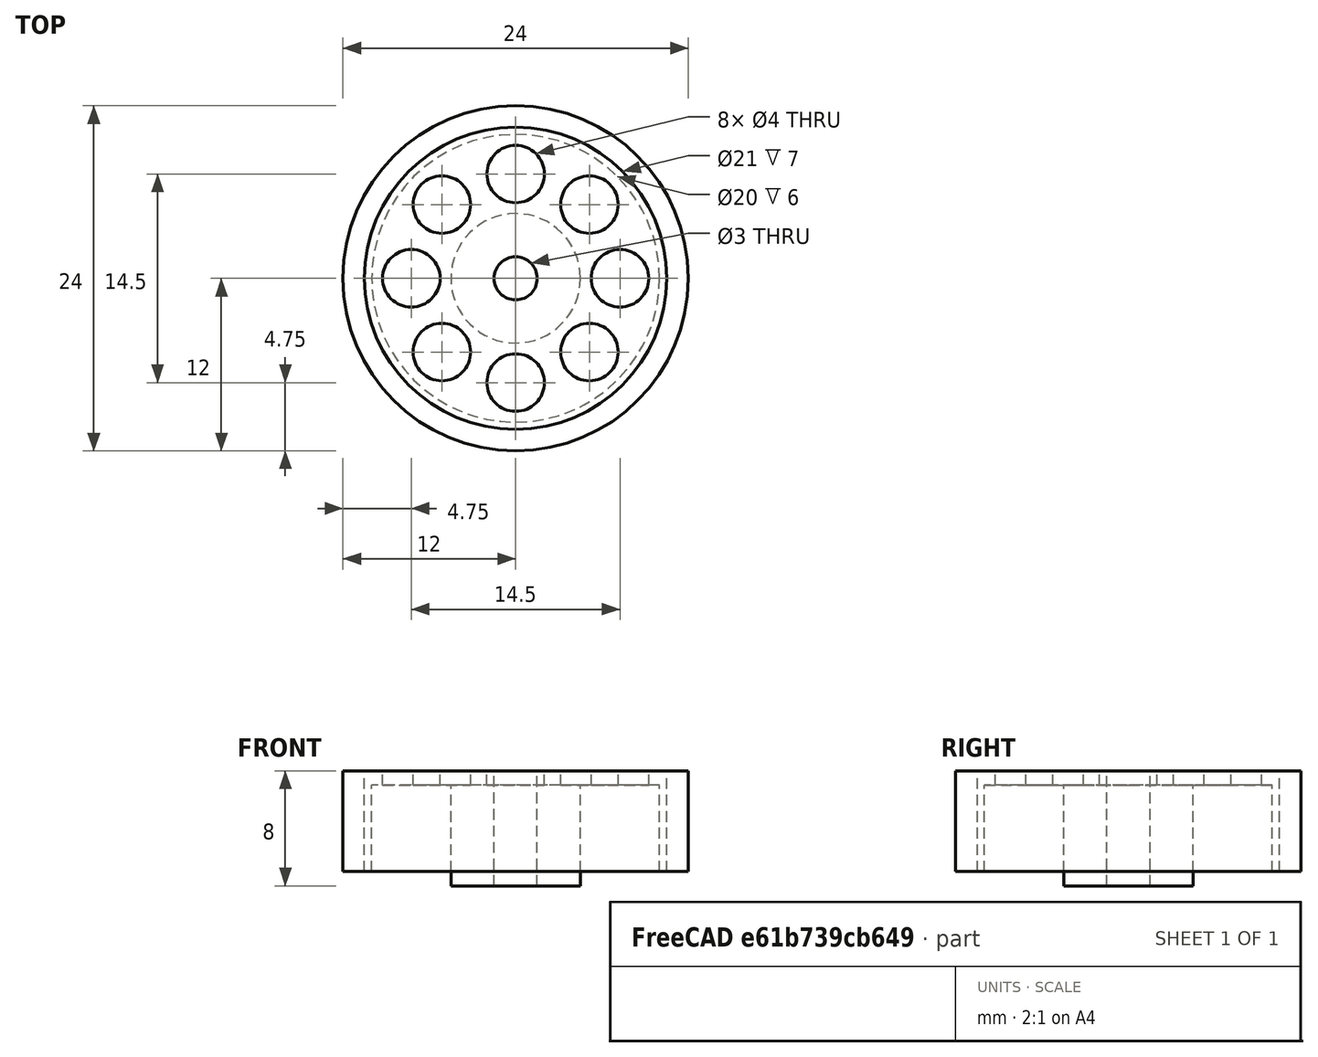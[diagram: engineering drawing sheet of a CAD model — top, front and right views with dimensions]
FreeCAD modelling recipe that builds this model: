
FCSTD DOCUMENT  (FreeCAD 0.14R3702 (Git))
Label: frontwheel
License: CC-BY 3.0
LicenseURL: http://creativecommons.org/licenses/by/3.0/
objects: Part::Cylinder×12, Part::Cut×5, Part::MultiFuse×4, Part::Compound×1
note: 22 computed .brp shape members not serialized (recipe doc carries the construction recipe); baked Part::Feature solids carry a one-line shape summary decoded from their .brp

FEATURE [Part::Cylinder] Cylinder
  Angle = 360
  Height = 1
  Radius = 10
FEATURE [Part::Cylinder] Cylinder001
  Angle = 360
  Height = 10
  Placement = pos=(0,7.25,0) rot=(0,0,1;1.5708rad)
  Radius = 2
FEATURE [Part::Cylinder] Cylinder002
  Angle = 360
  Height = 10
  Radius = 4.5
FEATURE [Part::Cylinder] Cylinder003
  Angle = 360
  Height = 10
  Placement = pos=(7.25,0,0) rot=(0,0,1;0.017453rad)
  Radius = 2
FEATURE [Part::Cylinder] Cylinder004
  Angle = 360
  Height = 10
  Placement = pos=(-7.25,0,0) rot=(0,0,1;1.5708rad)
  Radius = 2
FEATURE [Part::Cylinder] Cylinder005
  Angle = 360
  Height = 10
  Placement = pos=(0,-7.25,0) rot=(0,0,1;1.5708rad)
  Radius = 2
FEATURE [Part::MultiFuse] Fusion
  Shapes = -> [Cylinder001,Cylinder005,Cylinder004,Cylinder003]
FEATURE [Part::MultiFuse] Fusion002
  Placement = pos=(0,0,-5) rot=(0,0,1;0rad)
  Shapes = -> [Fusion]
FEATURE [Part::Cylinder] Cylinder010
  Angle = 360
  Height = 7
  Placement = pos=(0,0,-6) rot=(0,0,1;0rad)
  Radius = 10
FEATURE [Part::Cylinder] Cylinder011
  Angle = 360
  Height = 7
  Placement = pos=(0,0,-6) rot=(0,0,1;0rad)
  Radius = 12
FEATURE [Part::Cylinder] Cylinder012
  Angle = 360
  Height = 13
  Placement = pos=(0,0,-6) rot=(0,0,1;0rad)
  Radius = 10.5
FEATURE [Part::Cylinder] Cylinder013
  Angle = 360
  Height = 7
  Placement = pos=(0,0,-6) rot=(0,0,1;0rad)
  Radius = 10.5
FEATURE [Part::Cylinder] Cylinder014
  Angle = 360
  Height = 8
  Placement = pos=(0,0,-7) rot=(0,0,1;0rad)
  Radius = 4.5
FEATURE [Part::Cut] Cut002
  Base = -> Cylinder
  Tool = -> Cylinder002
FEATURE [Part::Cut] Cut003
  Base = -> Cut002
  Tool = -> Fusion002
FEATURE [Part::Cylinder] Cylinder015
  Angle = 360
  Height = 20
  Placement = pos=(0,0,-7) rot=(0,0,1;0rad)
  Radius = 1.5
FEATURE [Part::Cut] Cut
  Base = -> Cylinder011
  Tool = -> Cylinder012
FEATURE [Part::Cut] Cut004
  Base = -> Cylinder013
  Tool = -> Cylinder010
FEATURE [Part::MultiFuse] Fusion003
  Shapes = -> [Cut003,Cut004]
FEATURE [Part::Cut] Cut005
  Base = -> Cylinder014
  Tool = -> Cylinder015
FEATURE [Part::MultiFuse] Fusion004
  Shapes = -> [Fusion003,Cut005]
FEATURE [Part::Compound] Compound  label="FrontWheel"
  Links = -> [Cut,Fusion004]
